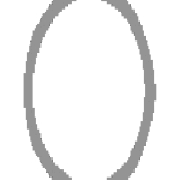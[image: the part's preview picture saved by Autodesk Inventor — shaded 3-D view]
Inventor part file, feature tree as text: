
AUTODESK INVENTOR PART (.ipt)
format: ipt  version: 2021 (Build 250183000, 183)  size: 112,128 bytes
history: native  units: in
note: dims shown in document units (in); Inventor stores cm internally (conversion verified against a paired STEP export)
features: other x4, sketch x3, plane x1
ambient origin geometry x8: Origin, YZ Plane, XZ Plane, XY Plane, X Axis, Y Axis, Z Axis, Center Point
bodies: Solid1 (feature_tree), Body (feature_tree)
feature tree (8):
  other  "Driven Length"
  other  "Frame Generator"
  other  "Start Plane"
  other  "End Plane"
  sketch  "Sketch"  dims[d2=25.5539in d4=-0.0in d5=25.5539in d6=0.12in d7=0.0in d8=90.0deg d9=25.5539in]
  sketch  "Sketch2"  dims[d0=1.0in]
  plane  "Work Plane3"
  sketch  "Sketch3"  dims[d1=0.065in]
